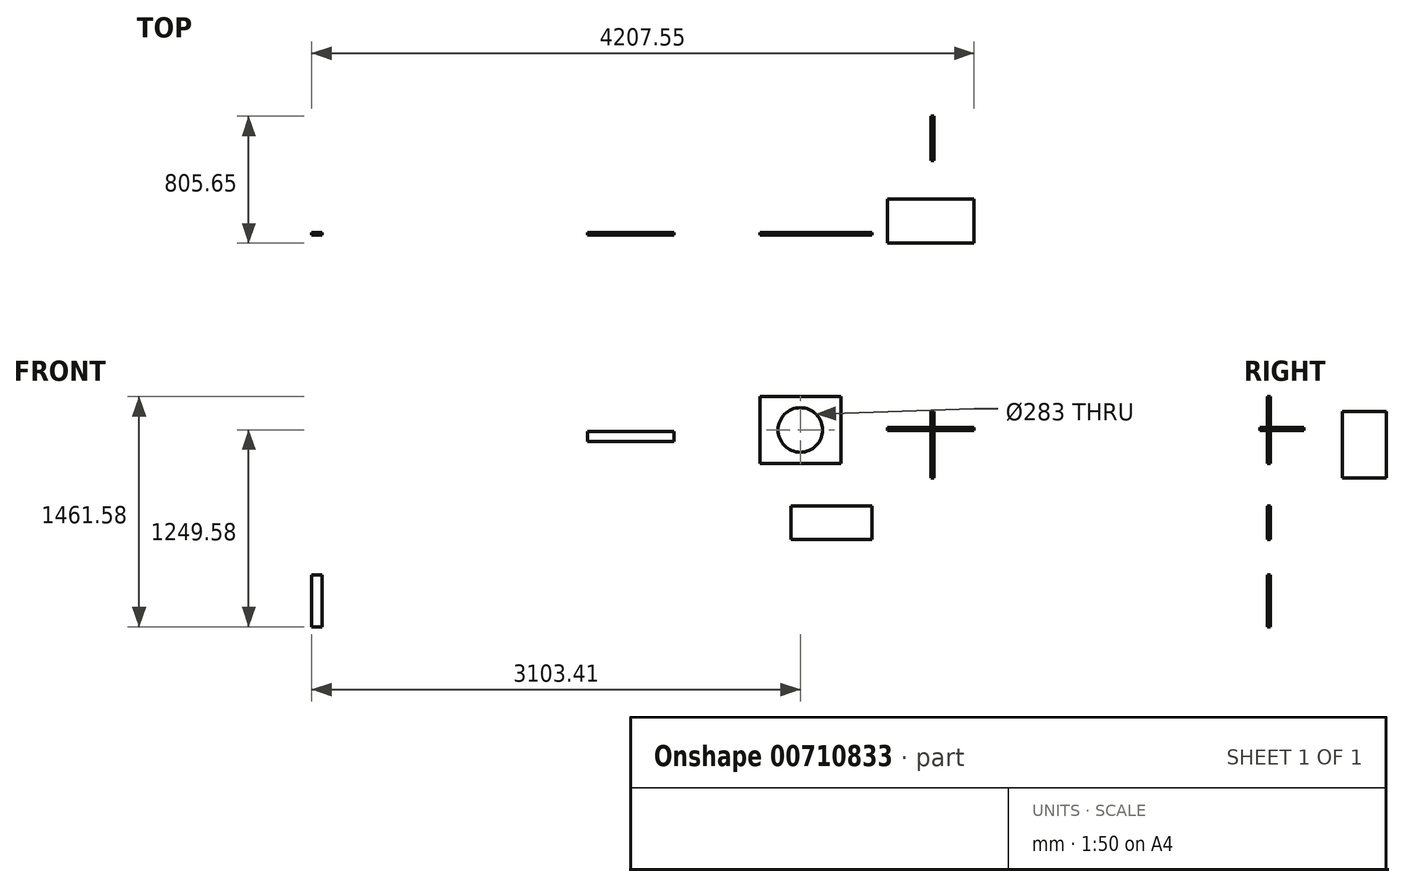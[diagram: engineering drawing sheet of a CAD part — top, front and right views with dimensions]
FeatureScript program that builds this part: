
annotation { "Feature Type Name" : "Feature", "Feature Type Description" : "" }
export const myFeature = defineFeature(function(context is Context, id is Id, definition is map)
    precondition{}
    {
        {
            var Q0;
            Q0=qCreatedBy(makeId("Top.planeOp"),FACE);
            var sketch = newSketch(context, id + "F0", { "sketchPlane" : qUnion([Q0])});
            skLineSegment(sketch, "E0.bottom", {"start": v(-275.76, 212.1) * mm, "end": v(274.24, 212.1) * mm});
            skLineSegment(sketch, "E0.top", {"start": v(-275.76, -67.9) * mm, "end": v(274.24, -67.9) * mm});
            skLineSegment(sketch, "E0.left", {"start": v(-275.76, 212.1) * mm, "end": v(-275.76, -67.9) * mm});
            skLineSegment(sketch, "E0.right", {"start": v(274.24, 212.1) * mm, "end": v(274.24, -67.9) * mm});
            skSolve(sketch);
        }
        {
            var Q0;
            Q0 = qSketchRegion(id + "F0", true);
            extrude(context, id + "F1", {"entities" : qUnion([Q0]), "depth" : 18 * mm, "offsetDistance" : 25 * mm});
        }
        {
            var Q0;
            Q0=qCreatedBy(makeId("Right.planeOp"),FACE);
            var sketch = newSketch(context, id + "F2", { "sketchPlane" : qUnion([Q0])});
            skLineSegment(sketch, "E1.bottom", {"start": v(737.75, 119.81) * mm, "end": v(457.75, 119.81) * mm});
            skLineSegment(sketch, "E1.top", {"start": v(737.75, -304.19) * mm, "end": v(457.75, -304.19) * mm});
            skLineSegment(sketch, "E1.left", {"start": v(737.75, 119.81) * mm, "end": v(737.75, -304.19) * mm});
            skLineSegment(sketch, "E1.right", {"start": v(457.75, 119.81) * mm, "end": v(457.75, -304.19) * mm});
            skSolve(sketch);
        }
        {
            var Q0;
            Q0=makeQuery(id+"F2.imprint","IMPRINT",FACE,{"disambiguationData":[TD([[makeQuery(id+"F2.imprint","IMPRINT",EDGE,{"derivedFrom":sQuery(id+"F2.wireOp",EDGE,"E1.bottom")}),1.0]])]});
            extrude(context, id + "F3", {"entities" : qUnion([Q0]), "depth" : 18 * mm, "offsetDistance" : 25 * mm});
        }
        {
            var Q0;
            Q0=qCreatedBy(makeId("Front.planeOp"),FACE);
            var sketch = newSketch(context, id + "F4", { "sketchPlane" : qUnion([Q0])});
            skLineSegment(sketch, "E2.bottom", {"start": v(-1086.9, 214.06) * mm, "end": v(-572.9, 214.06) * mm});
            skLineSegment(sketch, "E2.top", {"start": v(-1086.9, -209.94) * mm, "end": v(-572.9, -209.94) * mm});
            skLineSegment(sketch, "E2.left", {"start": v(-1086.9, 214.06) * mm, "end": v(-1086.9, -209.94) * mm});
            skLineSegment(sketch, "E2.right", {"start": v(-572.9, 214.06) * mm, "end": v(-572.9, -209.94) * mm});
            skSolve(sketch);
        }
        {
            var Q0;
            Q0 = qSketchRegion(id + "F4", true);
            extrude(context, id + "F5", {"entities" : qUnion([Q0]), "depth" : 18 * mm, "offsetDistance" : 25 * mm});
        }
        {
            var Q0;
            Q0=makeQuery(id+"F5.opExtrude","CAP_FACE",FACE,{"disambiguationData":[OSD([sQuery(id+"F4.wireOp",EDGE,"E2.bottom"),sQuery(id+"F4.wireOp",EDGE,"E2.top"),sQuery(id+"F4.wireOp",EDGE,"E2.left"),sQuery(id+"F4.wireOp",EDGE,"E2.right")])],"isStart":false});
            var sketch = newSketch(context, id + "F6", { "sketchPlane" : qUnion([Q0])});
            skLineSegment(sketch, "E3", {"start": v(-1086.9, 214.06) * mm, "end": v(-572.9, -209.94) * mm, "construction": true});
            skLineSegment(sketch, "E4", {"start": v(-572.9, 214.06) * mm, "end": v(-1086.9, -209.94) * mm, "construction": true});
            skPoint(sketch, "E5.centerSnap0", {"position": v(-829.9, 2.06) * mm});
            skCircle(sketch, "E6", {"center": v(-829.9, 2.06) * mm, "radius": 141.5 * mm});
            skSolve(sketch);
        }
        {
            var Q0;
            Q0=makeQuery(id+"F6.imprint","IMPRINT",FACE,{"disambiguationData":[TD([[makeQuery(id+"F6.imprint","IMPRINT",EDGE,{"derivedFrom":sQuery(id+"F6.wireOp",EDGE,"E6")}),1.0]])]});
            extrude(context, id + "F7", {"entities" : qUnion([Q0]), "operationType" : NewBodyOperationType.REMOVE, "endBound" : BoundingType.THROUGH_ALL, "oppositeDirection" : true, "depth" : 25 * mm, "offsetDistance" : 25 * mm});
        }
        {
            var Q0;
            Q0=qCreatedBy(makeId("Front.planeOp"),FACE);
            var sketch = newSketch(context, id + "F8", { "sketchPlane" : qUnion([Q0])});
            skLineSegment(sketch, "E7.bottom", {"start": v(-890.47, -481.82) * mm, "end": v(-376.47, -481.82) * mm});
            skLineSegment(sketch, "E7.top", {"start": v(-890.47, -693.82) * mm, "end": v(-376.47, -693.82) * mm});
            skLineSegment(sketch, "E7.left", {"start": v(-890.47, -481.82) * mm, "end": v(-890.47, -693.82) * mm});
            skLineSegment(sketch, "E7.right", {"start": v(-376.47, -481.82) * mm, "end": v(-376.47, -693.82) * mm});
            skSolve(sketch);
        }
        {
            var Q0;
            Q0=makeQuery(id+"F8.imprint","IMPRINT",FACE,{"disambiguationData":[TD([[makeQuery(id+"F8.imprint","IMPRINT",EDGE,{"derivedFrom":sQuery(id+"F8.wireOp",EDGE,"E7.bottom")}),-1.0]])]});
            extrude(context, id + "F9", {"entities" : qUnion([Q0]), "depth" : 18 * mm, "offsetDistance" : 25 * mm});
        }
        {
            var Q0;
            Q0=qCreatedBy(makeId("Front.planeOp"),FACE);
            var sketch = newSketch(context, id + "F10", { "sketchPlane" : qUnion([Q0])});
            skLineSegment(sketch, "E8.bottom", {"start": v(-2182.8, -6.56) * mm, "end": v(-1632.8, -6.56) * mm});
            skLineSegment(sketch, "E8.top", {"start": v(-2182.8, -71.56) * mm, "end": v(-1632.8, -71.56) * mm});
            skLineSegment(sketch, "E8.left", {"start": v(-2182.8, -6.56) * mm, "end": v(-2182.8, -71.56) * mm});
            skLineSegment(sketch, "E8.right", {"start": v(-1632.8, -6.56) * mm, "end": v(-1632.8, -71.56) * mm});
            skSolve(sketch);
        }
        {
            var Q0;
            Q0=makeQuery(id+"F10.imprint","IMPRINT",FACE,{"disambiguationData":[TD([[makeQuery(id+"F10.imprint","IMPRINT",EDGE,{"derivedFrom":sQuery(id+"F10.wireOp",EDGE,"E8.bottom")}),-1.0]])]});
            extrude(context, id + "F11", {"entities" : qUnion([Q0]), "depth" : 18 * mm, "offsetDistance" : 25 * mm});
        }
        {
            var Q0;
            Q0=qCreatedBy(makeId("Front.planeOp"),FACE);
            var sketch = newSketch(context, id + "F12", { "sketchPlane" : qUnion([Q0])});
            skLineSegment(sketch, "E9.bottom", {"start": v(-3933.31, -917.52) * mm, "end": v(-3868.31, -917.52) * mm});
            skLineSegment(sketch, "E9.top", {"start": v(-3933.31, -1247.52) * mm, "end": v(-3868.31, -1247.52) * mm});
            skLineSegment(sketch, "E9.left", {"start": v(-3933.31, -917.52) * mm, "end": v(-3933.31, -1247.52) * mm});
            skLineSegment(sketch, "E9.right", {"start": v(-3868.31, -917.52) * mm, "end": v(-3868.31, -1247.52) * mm});
            skSolve(sketch);
        }
        {
            var Q0;
            Q0=makeQuery(id+"F12.imprint","IMPRINT",FACE,{"disambiguationData":[TD([[makeQuery(id+"F12.imprint","IMPRINT",EDGE,{"derivedFrom":sQuery(id+"F12.wireOp",EDGE,"E9.bottom")}),-1.0]])]});
            extrude(context, id + "F13", {"entities" : qUnion([Q0]), "depth" : 18 * mm, "offsetDistance" : 25 * mm});
        }
    });
